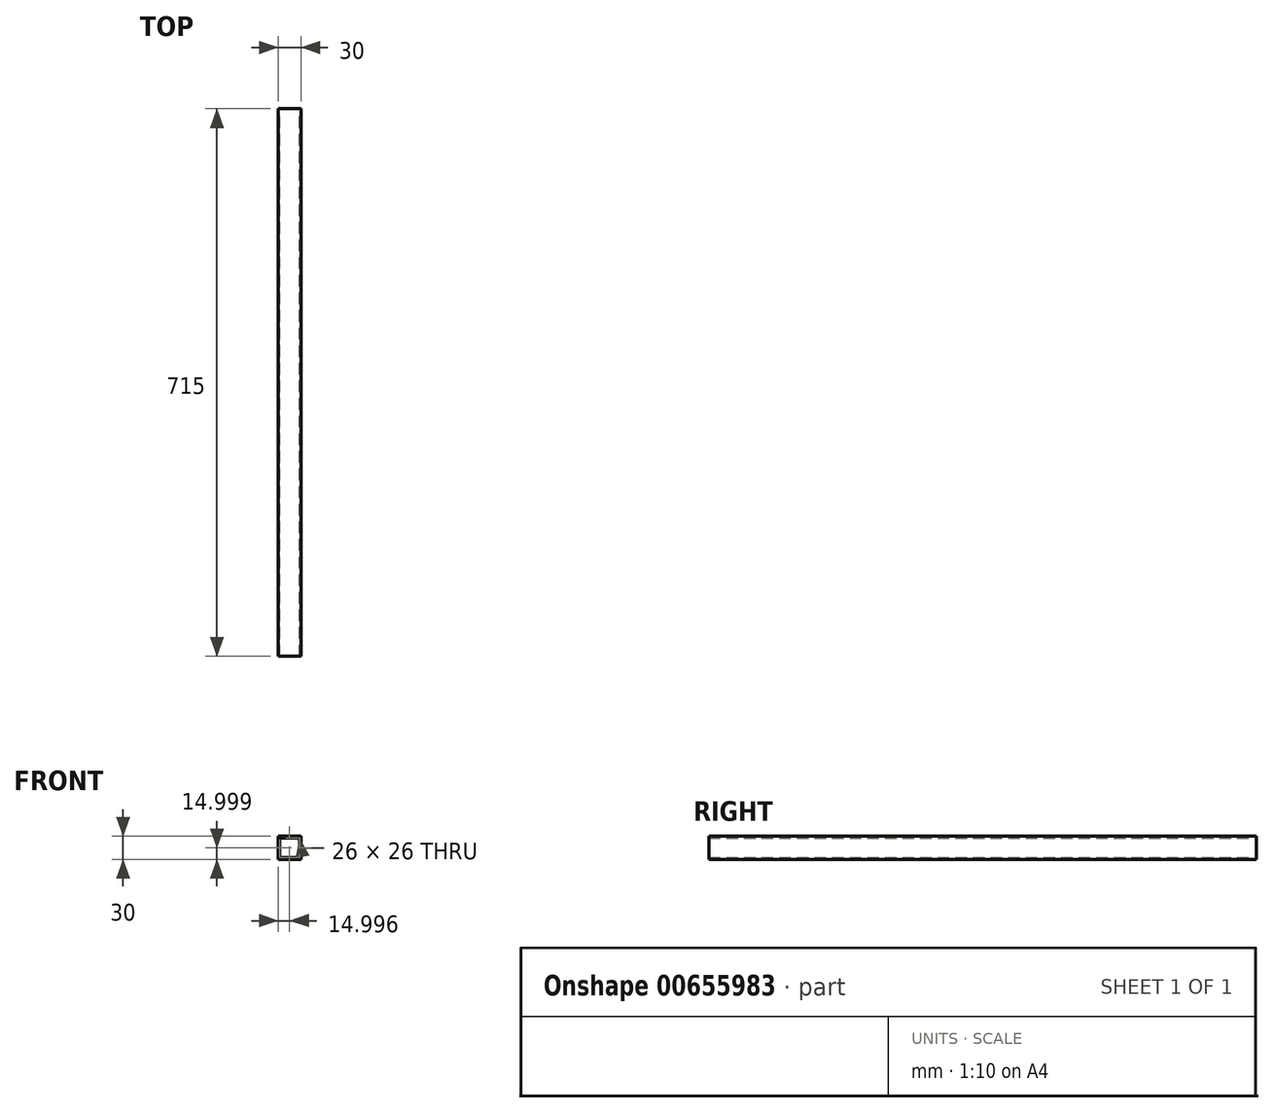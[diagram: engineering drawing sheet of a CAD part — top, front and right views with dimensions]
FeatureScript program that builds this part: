
annotation { "Feature Type Name" : "Feature", "Feature Type Description" : "" }
export const myFeature = defineFeature(function(context is Context, id is Id, definition is map)
    precondition{}
    {
        {
            var Q0;
            Q0=qCreatedBy(makeId("Front.planeOp"),FACE);
            var sketch = newSketch(context, id + "F0", { "sketchPlane" : qUnion([Q0])});
            skLineSegment(sketch, "E0.bottom", {"start": v(19.24, 9.55) * mm, "end": v(49.24, 9.55) * mm});
            skLineSegment(sketch, "E0.top", {"start": v(19.24, -20.45) * mm, "end": v(49.24, -20.45) * mm});
            skLineSegment(sketch, "E0.left", {"start": v(19.24, 9.55) * mm, "end": v(19.24, -20.45) * mm});
            skLineSegment(sketch, "E0.right", {"start": v(49.24, 9.55) * mm, "end": v(49.24, -20.45) * mm});
            skLineSegment(sketch, "E1.0", {"start": v(21.24, 7.55) * mm, "end": v(47.24, 7.55) * mm});
            skLineSegment(sketch, "E1.1", {"start": v(21.24, 7.55) * mm, "end": v(21.24, -18.45) * mm});
            skLineSegment(sketch, "E1.2", {"start": v(21.24, -18.45) * mm, "end": v(47.24, -18.45) * mm});
            skLineSegment(sketch, "E1.3", {"start": v(47.24, 7.55) * mm, "end": v(47.24, -18.45) * mm});
            skSolve(sketch);
        }
        {
            var Q0;
            Q0=makeQuery(id+"F0.imprint","IMPRINT",FACE,{"disambiguationData":[TD([[makeQuery(id+"F0.imprint","IMPRINT",EDGE,{"derivedFrom":sQuery(id+"F0.wireOp",EDGE,"E0.bottom")}),-1.0]])]});
            extrude(context, id + "F1", {"entities" : qUnion([Q0]), "depth" : 715 * mm, "offsetDistance" : 25.4 * mm});
        }
    });
